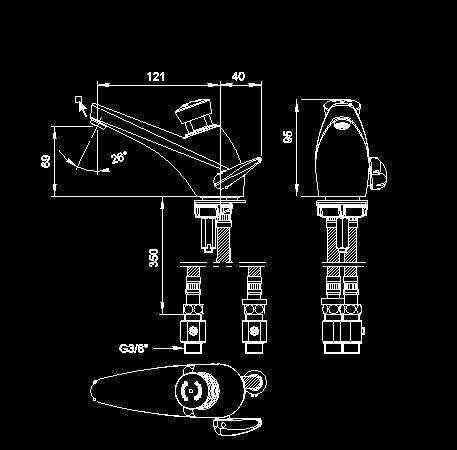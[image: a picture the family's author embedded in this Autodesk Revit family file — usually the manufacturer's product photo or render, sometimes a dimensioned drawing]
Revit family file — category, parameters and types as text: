
# Revit family: Robinet mitigeur temporisé pour lavabo-Presto3000-68302
name_source: partatom
category: Plumbing Fixtures
revit_build: Autodesk Revit MEP 2014 (Build: 20131024_2115(x64)
units: mm (PartAtom-declared; Revit-internal decimal feet)

## types (1)
- Robinet mitigeur temporisé pour lavabo-Presto3000-68302
    BIMobject category = Sanitary
    CW Inlet = 10 mm  [stored 0.0328084 ft]
    Date of publishing = 2011-07-27
    Default Elevation = 1219 mm
    Design country = France
    Durée d'écoulement (± 5 secondes) = 15.0 s
    Débit (Réglage 4 positions) = 3 l/mn à 3 bars
    Edition number = 1
    Height = 95 mm
    IFC Classification = Space Heater
    Manufacturer = PRESTO LES ROBINETS
    Manufacturer country = France
    Manufacturer name = Presto
    Material main = Brass
    Material secondary = Chrome
    Model = 68032
    Nominal height = 95.00
    Nominal width = 0.00
    Pression d'utilisation recommandée = 1 à 5 bars
    Product Guid = 5bece58f-72c9-4f5f-af73-2e9d05402475
    Product SKU = 68032
    Product data url = http://bimobject.com
    Product family = Mixer Tap
    Product group = Deck-mounted
    QR code = http://bimobject.com
    Résistance thermique (30 minutes) = 75 °C
    UNSPSC Code = 301815
    URL to Data = http://www.prestodatashare.com
    Warranty = 10
    Weight Net (Kg) = 0

note: [stored X ft] marks values corroborated as IEEE doubles in the binary element streams (Revit-internal decimal feet)

## geometry (parser evidence)
native form markers: Sweep x5
no freeform markers — native parametric forms only
